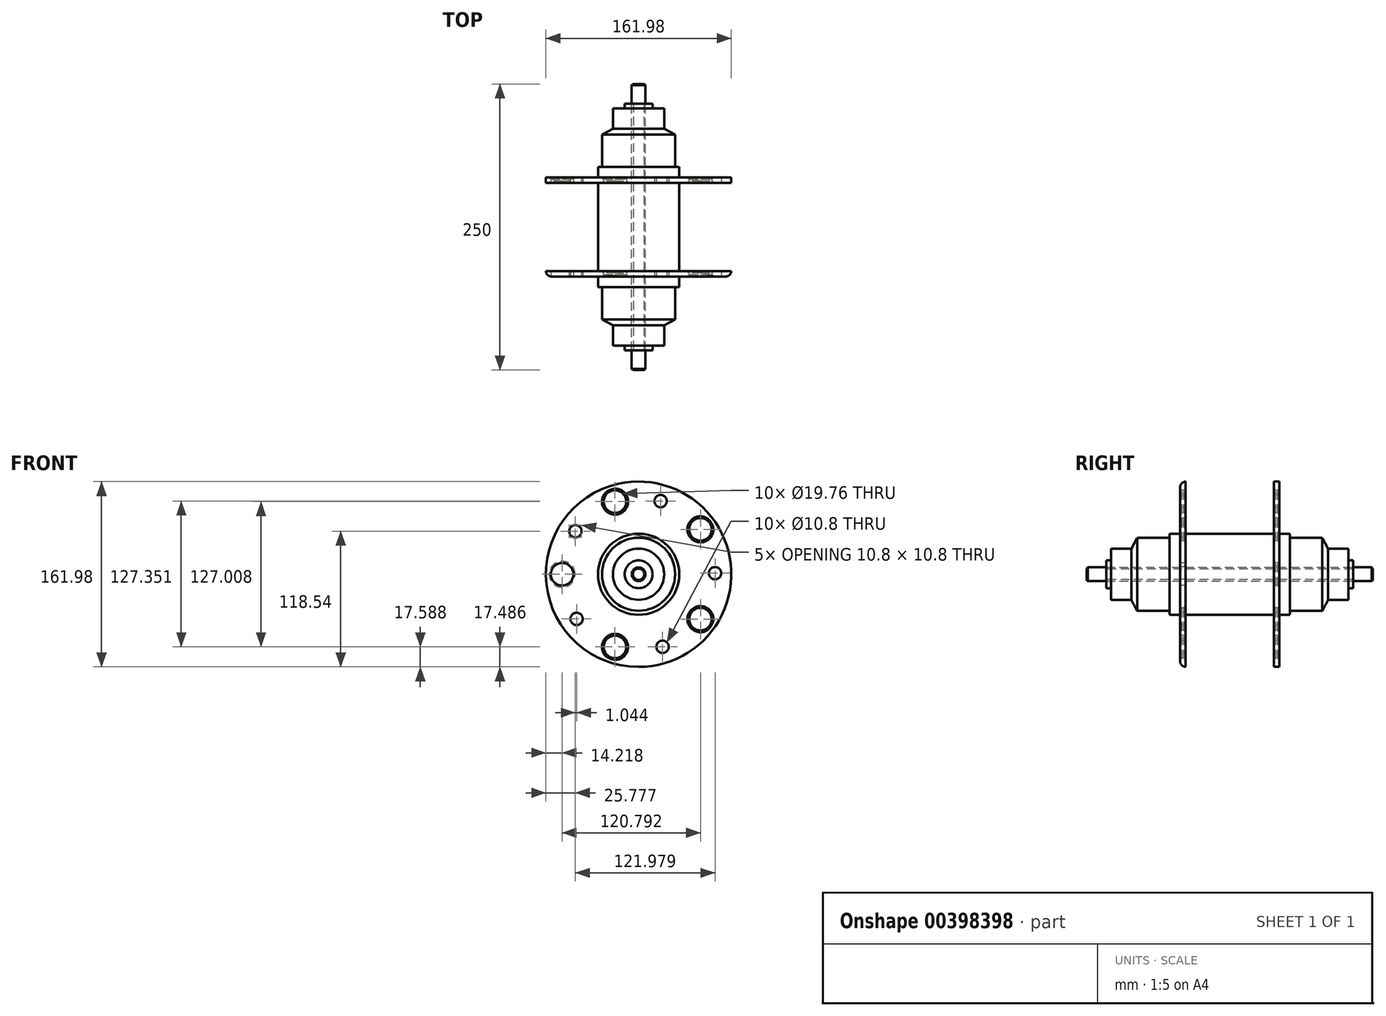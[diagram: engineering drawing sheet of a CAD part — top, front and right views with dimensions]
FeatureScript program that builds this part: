
annotation { "Feature Type Name" : "Feature", "Feature Type Description" : "" }
export const myFeature = defineFeature(function(context is Context, id is Id, definition is map)
    precondition{}
    {
        {
            var Q0;
            Q0=qCreatedBy(makeId("Front.planeOp"),FACE);
            var sketch = newSketch(context, id + "F0", { "sketchPlane" : qUnion([Q0])});
            skCircle(sketch, "E0", {"center": v(0, 0) * mm, "radius": 6 * mm});
            skSolve(sketch);
        }
        {
            var Q0;
            Q0 = qSketchRegion(id + "F0", true);
            extrude(context, id + "F1", {"entities" : qUnion([Q0]), "endBound" : BoundingType.SYMMETRIC, "depth" : 250 * mm});
        }
        {
            var Q0;
            Q0=qCreatedBy(makeId("Right.planeOp"),FACE);
            var sketch = newSketch(context, id + "F2", { "sketchPlane" : qUnion([Q0])});
            skLineSegment(sketch, "E1", {"start": v(-139.45, 0) * mm, "end": v(142.74, 0) * mm, "construction": true});
            skLineSegment(sketch, "E2", {"start": v(0, -48.34) * mm, "end": v(0, 50.11) * mm, "construction": true});
            skSolve(sketch);
        }
        {
            var Q0;
            Q0=qCreatedBy(makeId("Right.planeOp"),FACE);
            var sketch = newSketch(context, id + "F3", { "sketchPlane" : qUnion([Q0])});
            skLineSegment(sketch, "E3", {"start": v(0, 4.56) * mm, "end": v(107.81, 4.56) * mm});
            skLineSegment(sketch, "E4", {"start": v(107.81, 4.56) * mm, "end": v(107.81, 12.15) * mm});
            skLineSegment(sketch, "E5", {"start": v(107.81, 12.15) * mm, "end": v(103.51, 12.15) * mm});
            skLineSegment(sketch, "E6", {"start": v(103.51, 12.15) * mm, "end": v(103.51, 22.37) * mm});
            skLineSegment(sketch, "E7", {"start": v(103.51, 22.37) * mm, "end": v(85.9, 22.37) * mm});
            skLineSegment(sketch, "E8", {"start": v(85.9, 22.37) * mm, "end": v(80.87, 31.95) * mm});
            skLineSegment(sketch, "E9", {"start": v(80.87, 31.95) * mm, "end": v(52.64, 31.95) * mm});
            skLineSegment(sketch, "E10", {"start": v(52.64, 31.95) * mm, "end": v(52.64, 35.48) * mm});
            skLineSegment(sketch, "E11", {"start": v(52.64, 35.48) * mm, "end": v(43.28, 35.48) * mm});
            skLineSegment(sketch, "E12", {"start": v(43.28, 35.48) * mm, "end": v(43.28, 80.99) * mm});
            skLineSegment(sketch, "E13", {"start": v(43.28, 80.99) * mm, "end": v(38.72, 80.99) * mm});
            skLineSegment(sketch, "E14", {"start": v(38.72, 80.99) * mm, "end": v(38.72, 35.48) * mm});
            skLineSegment(sketch, "E15", {"start": v(38.72, 35.48) * mm, "end": v(0, 35.48) * mm});
            skLineSegment(sketch, "E16.MirrorCS", {"start": v(-107.81, 12.15) * mm, "end": v(-103.51, 12.15) * mm});
            skLineSegment(sketch, "E17.MirrorCS", {"start": v(-103.51, 22.37) * mm, "end": v(-85.9, 22.37) * mm});
            skLineSegment(sketch, "E18.MirrorCS", {"start": v(-43.28, 80.99) * mm, "end": v(-38.72, 80.99) * mm});
            skLineSegment(sketch, "E19.MirrorCS", {"start": v(0, 4.56) * mm, "end": v(-107.81, 4.56) * mm});
            skLineSegment(sketch, "E20.MirrorCS", {"start": v(-107.81, 4.56) * mm, "end": v(-107.81, 12.15) * mm});
            skLineSegment(sketch, "E21.MirrorCS", {"start": v(-38.72, 35.48) * mm, "end": v(0, 35.48) * mm});
            skLineSegment(sketch, "E22.MirrorCS", {"start": v(-103.51, 12.15) * mm, "end": v(-103.51, 22.37) * mm});
            skLineSegment(sketch, "E23.MirrorCS", {"start": v(-38.72, 80.99) * mm, "end": v(-38.72, 35.48) * mm});
            skLineSegment(sketch, "E24.MirrorCS", {"start": v(-52.64, 35.48) * mm, "end": v(-43.28, 35.48) * mm});
            skLineSegment(sketch, "E25.MirrorCS", {"start": v(-52.64, 31.95) * mm, "end": v(-52.64, 35.48) * mm});
            skLineSegment(sketch, "E26.MirrorCS", {"start": v(-43.28, 35.48) * mm, "end": v(-43.28, 80.99) * mm});
            skLineSegment(sketch, "E27.MirrorCS", {"start": v(-85.9, 22.37) * mm, "end": v(-80.87, 31.95) * mm});
            skLineSegment(sketch, "E28.MirrorCS", {"start": v(-80.87, 31.95) * mm, "end": v(-52.64, 31.95) * mm});
            skSolve(sketch);
        }
        {
            var Q0;
            Q0=makeQuery(id+"F3.imprint","IMPRINT",FACE,{"disambiguationData":[TD([[makeQuery(id+"F3.imprint","IMPRINT",EDGE,{"derivedFrom":sQuery(id+"F3.wireOp",EDGE,"E3")}),1.0]])]});
            var Q1;
            Q1=sQuery(id+"F3.wireOp",EDGE,"E26.MirrorCS");
            var Q2;
            Q2=sQuery(id+"F3.wireOp",EDGE,"E28.MirrorCS");
            var Q3;
            Q3=sQuery(id+"F3.wireOp",EDGE,"E21.MirrorCS");
            var Q4;
            Q4=sQuery(id+"F3.wireOp",EDGE,"E23.MirrorCS");
            var Q5;
            Q5=sQuery(id+"F3.wireOp",EDGE,"E25.MirrorCS");
            var Q6;
            Q6=sQuery(id+"F3.wireOp",EDGE,"E24.MirrorCS");
            var Q7;
            Q7=sQuery(id+"F3.wireOp",EDGE,"E27.MirrorCS");
            var Q8;
            Q8=sQuery(id+"F3.wireOp",EDGE,"E15");
            var Q9;
            Q9=sQuery(id+"F3.wireOp",EDGE,"E14");
            var Q10;
            Q10=sQuery(id+"F3.wireOp",EDGE,"E12");
            var Q11;
            Q11=sQuery(id+"F3.wireOp",EDGE,"E11");
            var Q12;
            Q12=sQuery(id+"F3.wireOp",EDGE,"E10");
            var Q13;
            Q13=sQuery(id+"F3.wireOp",EDGE,"E9");
            var Q14;
            Q14=sQuery(id+"F3.wireOp",EDGE,"E8");
            var Q15;
            Q15=sQuery(id+"F3.wireOp",EDGE,"E17.MirrorCS");
            var Q16;
            Q16=sQuery(id+"F3.wireOp",EDGE,"E13");
            var Q17;
            Q17=sQuery(id+"F3.wireOp",EDGE,"E18.MirrorCS");
            var Q18;
            Q18=sQuery(id+"F3.wireOp",EDGE,"E7");
            var Q19;
            Q19=sQuery(id+"F2.wireOp",EDGE,"E1");
            revolve(context, id + "F4", {"entities" : qUnion([Q0]), "surfaceEntities" : qUnion([Q1, Q2, Q3, Q4, Q5, Q6, Q7, Q8, Q9, Q10, Q11, Q12, Q13, Q14, Q15, Q16, Q17, Q18]), "axis" : qUnion([Q19]), "revolveType" : RevolveType.FULL});
        }
        {
            var Q0;
            Q0=makeQuery(id+"F4.opRevolve","SWEPT_FACE",FACE,{"disambiguationData":[OSD([sQuery(id+"F3.wireOp",EDGE,"E26.MirrorCS")])]});
            var sketch = newSketch(context, id + "F5", { "sketchPlane" : qUnion([Q0])});
            skCircle(sketch, "E29", {"center": v(0, 0) * mm, "radius": 66.77 * mm, "construction": true});
            skLineSegment(sketch, "E30", {"start": v(-116.8, 0) * mm, "end": v(114.85, 0) * mm, "construction": true});
            skLineSegment(sketch, "E31", {"start": v(0, 86.33) * mm, "end": v(0, -94.06) * mm, "construction": true});
            skCircle(sketch, "E32", {"center": v(-66.77, 0) * mm, "radius": 9.88 * mm});
            skCircle(sketch, "E33.1.0", {"center": v(-20.63, -63.5) * mm, "radius": 9.88 * mm});
            skCircle(sketch, "E34.1.2.0", {"center": v(54.02, -39.25) * mm, "radius": 9.88 * mm});
            skCircle(sketch, "E34.1.3.0", {"center": v(54.02, 39.25) * mm, "radius": 9.88 * mm});
            skCircle(sketch, "E34.1.4.0", {"center": v(-20.63, 63.5) * mm, "radius": 9.88 * mm});
            skCircle(sketch, "E35", {"center": v(-55.21, 37.55) * mm, "radius": 5.4 * mm});
            skCircle(sketch, "E36.1.0", {"center": v(19.2, 63.95) * mm, "radius": 5.4 * mm});
            skCircle(sketch, "E36.2.0", {"center": v(66.77, 0.9) * mm, "radius": 5.4 * mm});
            skCircle(sketch, "E36.3.0", {"center": v(20.94, -63.4) * mm, "radius": 5.4 * mm});
            skCircle(sketch, "E36.4.0", {"center": v(-54.17, -39.04) * mm, "radius": 5.4 * mm});
            skLineSegment(sketch, "E36.anchor1", {"start": v(0, 0) * mm, "end": v(-55.21, 37.55) * mm, "construction": true});
            skLineSegment(sketch, "E36.anchor2", {"start": v(0, 0) * mm, "end": v(-54.17, -39.04) * mm, "construction": true});
            skSolve(sketch);
        }
        {
            var Q0;
            Q0 = qSketchRegion(id + "F5", true);
            extrude(context, id + "F6", {"entities" : qUnion([Q0]), "operationType" : NewBodyOperationType.REMOVE, "endBound" : BoundingType.THROUGH_ALL, "oppositeDirection" : true, "depth" : 25 * mm});
        }
        {
            var Q0;
            Q0=makeQuery(id+"F6.boolean.opBoolean","COPY",FACE,{"disambiguationData":[TD([makeQuery(id+"F4.opRevolve","SWEPT_FACE",FACE,{"disambiguationData":[OSD([sQuery(id+"F3.wireOp",EDGE,"E23.MirrorCS")])]})])],"derivedFrom":makeQuery(id+"F6.opExtrude","SWEPT_FACE",FACE,{"disambiguationData":[OSD([sQuery(id+"F5.wireOp",EDGE,"E34.1.4.0")])]})});
            var Q1;
            Q1=makeQuery(id+"F6.boolean.opBoolean","COPY",EDGE,{"derivedFrom":makeQuery(id+"F6.opExtrude","CAP_EDGE",EDGE,{"disambiguationData":[OSD([sQuery(id+"F5.wireOp",EDGE,"E32")])],"isStart":true})});
            var Q2;
            Q2=makeQuery(id+"F6.boolean.opBoolean","COPY",FACE,{"disambiguationData":[TD([makeQuery(id+"F4.opRevolve","SWEPT_FACE",FACE,{"disambiguationData":[OSD([sQuery(id+"F3.wireOp",EDGE,"E23.MirrorCS")])]})])],"derivedFrom":makeQuery(id+"F6.opExtrude","SWEPT_FACE",FACE,{"disambiguationData":[OSD([sQuery(id+"F5.wireOp",EDGE,"E33.1.0")])]})});
            var Q3;
            Q3=makeQuery(id+"F6.boolean.opBoolean","COPY",FACE,{"disambiguationData":[TD([makeQuery(id+"F4.opRevolve","SWEPT_FACE",FACE,{"disambiguationData":[OSD([sQuery(id+"F3.wireOp",EDGE,"E23.MirrorCS")])]})])],"derivedFrom":makeQuery(id+"F6.opExtrude","SWEPT_FACE",FACE,{"disambiguationData":[OSD([sQuery(id+"F5.wireOp",EDGE,"E34.1.2.0")])]})});
            var Q4;
            Q4=makeQuery(id+"F6.boolean.opBoolean","COPY",FACE,{"disambiguationData":[TD([makeQuery(id+"F4.opRevolve","SWEPT_FACE",FACE,{"disambiguationData":[OSD([sQuery(id+"F3.wireOp",EDGE,"E23.MirrorCS")])]})])],"derivedFrom":makeQuery(id+"F6.opExtrude","SWEPT_FACE",FACE,{"disambiguationData":[OSD([sQuery(id+"F5.wireOp",EDGE,"E34.1.3.0")])]})});
            var Q5;
            Q5=makeQuery(id+"F6.boolean.opBoolean","COPY",FACE,{"disambiguationData":[TD([makeQuery(id+"F4.opRevolve","SWEPT_FACE",FACE,{"disambiguationData":[OSD([sQuery(id+"F3.wireOp",EDGE,"E12")])]})])],"derivedFrom":makeQuery(id+"F6.opExtrude","SWEPT_FACE",FACE,{"disambiguationData":[OSD([sQuery(id+"F5.wireOp",EDGE,"E33.1.0")])]})});
            var Q6;
            Q6=makeQuery(id+"F6.boolean.opBoolean","COPY",FACE,{"disambiguationData":[TD([makeQuery(id+"F4.opRevolve","SWEPT_FACE",FACE,{"disambiguationData":[OSD([sQuery(id+"F3.wireOp",EDGE,"E12")])]})])],"derivedFrom":makeQuery(id+"F6.opExtrude","SWEPT_FACE",FACE,{"disambiguationData":[OSD([sQuery(id+"F5.wireOp",EDGE,"E34.1.2.0")])]})});
            var Q7;
            Q7=makeQuery(id+"F6.boolean.opBoolean","COPY",FACE,{"disambiguationData":[TD([makeQuery(id+"F4.opRevolve","SWEPT_FACE",FACE,{"disambiguationData":[OSD([sQuery(id+"F3.wireOp",EDGE,"E12")])]})])],"derivedFrom":makeQuery(id+"F6.opExtrude","SWEPT_FACE",FACE,{"disambiguationData":[OSD([sQuery(id+"F5.wireOp",EDGE,"E32")])]})});
            var Q8;
            Q8=makeQuery(id+"F6.boolean.opBoolean","COPY",FACE,{"disambiguationData":[TD([makeQuery(id+"F4.opRevolve","SWEPT_FACE",FACE,{"disambiguationData":[OSD([sQuery(id+"F3.wireOp",EDGE,"E12")])]})])],"derivedFrom":makeQuery(id+"F6.opExtrude","SWEPT_FACE",FACE,{"disambiguationData":[OSD([sQuery(id+"F5.wireOp",EDGE,"E34.1.4.0")])]})});
            var Q9;
            Q9=makeQuery(id+"F6.boolean.opBoolean","COPY",FACE,{"disambiguationData":[TD([makeQuery(id+"F4.opRevolve","SWEPT_FACE",FACE,{"disambiguationData":[OSD([sQuery(id+"F3.wireOp",EDGE,"E12")])]})])],"derivedFrom":makeQuery(id+"F6.opExtrude","SWEPT_FACE",FACE,{"disambiguationData":[OSD([sQuery(id+"F5.wireOp",EDGE,"E34.1.3.0")])]})});
            chamfer(context, id + "F7", {"entities" : qUnion([Q0, Q1, Q2, Q3, Q4, Q5, Q6, Q7, Q8, Q9]), "width" : 1.5 * mm, "tangentPropagation" : true});
        }
        {
            var Q0;
            Q0=makeQuery(id+"F1.opExtrude","CAP_FACE",FACE,{"disambiguationData":[OSD([sQuery(id+"F0.wireOp",EDGE,"E0")])],"isStart":true});
            var Q1;
            Q1=makeQuery(id+"F1.opExtrude","CAP_FACE",FACE,{"disambiguationData":[OSD([sQuery(id+"F0.wireOp",EDGE,"E0")])],"isStart":false});
            chamfer(context, id + "F8", {"entities" : qUnion([Q0, Q1]), "width" : 1 * mm, "tangentPropagation" : true});
        }
        {
            var Q0;
            Q0=makeQuery(id+"F4.opRevolve","SWEPT_EDGE",EDGE,{"disambiguationData":[OSD([sQuery(id+"F3.wireOp",EDGE,"E18.MirrorCS"),sQuery(id+"F3.wireOp",EDGE,"E26.MirrorCS")])]});
            fillet(context, id + "F9", {"entities" : qUnion([Q0]), "radius" : 5 * mm, "tangentPropagation" : true, "allowEdgeOverflow" : false});
        }
    });
